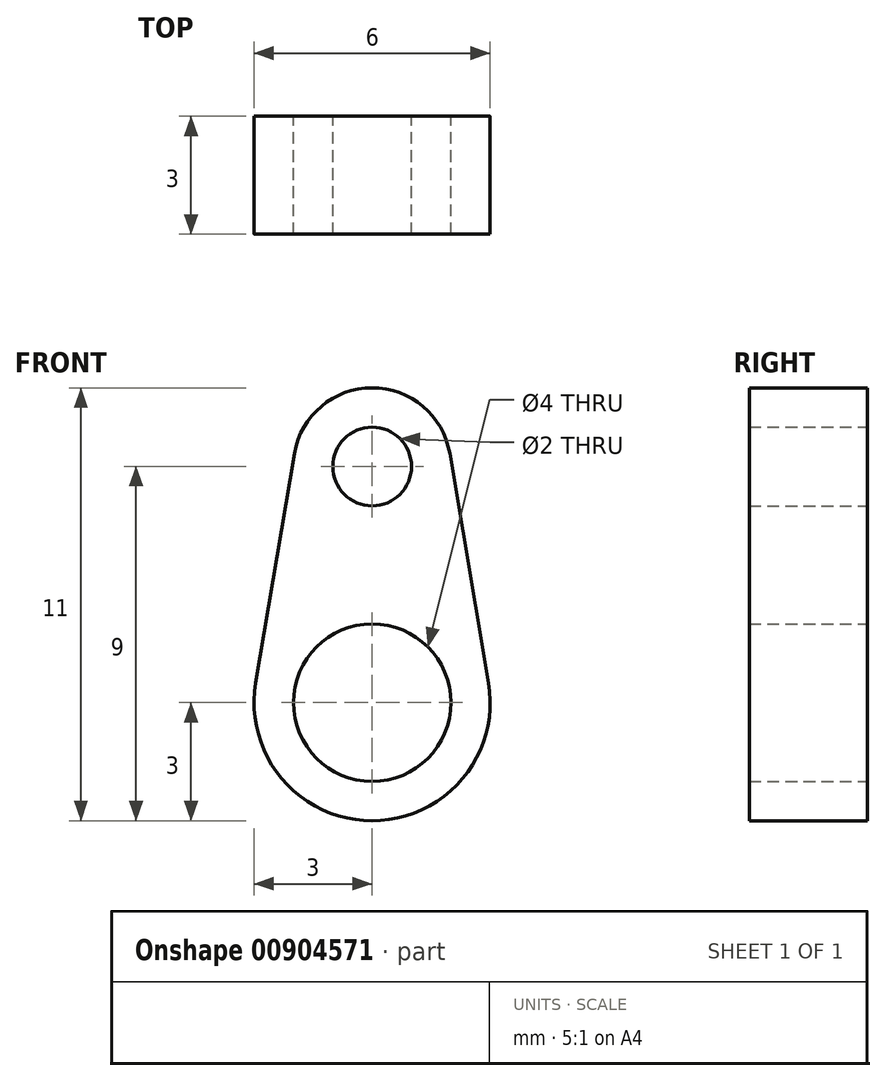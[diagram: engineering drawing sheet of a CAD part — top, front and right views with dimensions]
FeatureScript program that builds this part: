
annotation { "Feature Type Name" : "Feature", "Feature Type Description" : "" }
export const myFeature = defineFeature(function(context is Context, id is Id, definition is map)
    precondition{}
    {
        {
            var Q0;
            Q0=qCreatedBy(makeId("Front.planeOp"),FACE);
            var sketch = newSketch(context, id + "F0", { "sketchPlane" : qUnion([Q0])});
            skArc(sketch, "E0", {"start": v(1.97, 6.33) * mm, "mid": v(-0.17, 8) * mm, "end": v(-2, 6) * mm});
            skCircle(sketch, "E1", {"center": v(0, 0) * mm, "radius": 2 * mm});
            skLineSegment(sketch, "E2", {"start": v(1.97, 6.33) * mm, "end": v(2.96, 0.5) * mm});
            skArc(sketch, "E3", {"start": v(-2.96, 0.5) * mm, "mid": v(0, -3) * mm, "end": v(2.96, 0.5) * mm});
            skLineSegment(sketch, "E4.MirrorCS", {"start": v(-1.97, 6.33) * mm, "end": v(-2.96, 0.5) * mm});
            skPoint(sketch, "E5.orphan", {"position": v(-1.64, 8.31) * mm});
            skPoint(sketch, "E6.orphan", {"position": v(1.64, 8.31) * mm});
            skPoint(sketch, "E7.orphan", {"position": v(3.5, -2.66) * mm});
            skPoint(sketch, "E8.orphan", {"position": v(-3.5, -2.66) * mm});
            skCircle(sketch, "E9", {"center": v(0, 6) * mm, "radius": 1 * mm});
            skPoint(sketch, "E10.orphan", {"position": v(2, 6) * mm});
            skSolve(sketch);
        }
        {
            var Q0;
            Q0 = qSketchRegion(id + "F0", true);
            extrude(context, id + "F1", {"entities" : qUnion([Q0]), "endBound" : BoundingType.SYMMETRIC, "depth" : 3 * mm, "offsetDistance" : 25 * mm});
        }
    });
